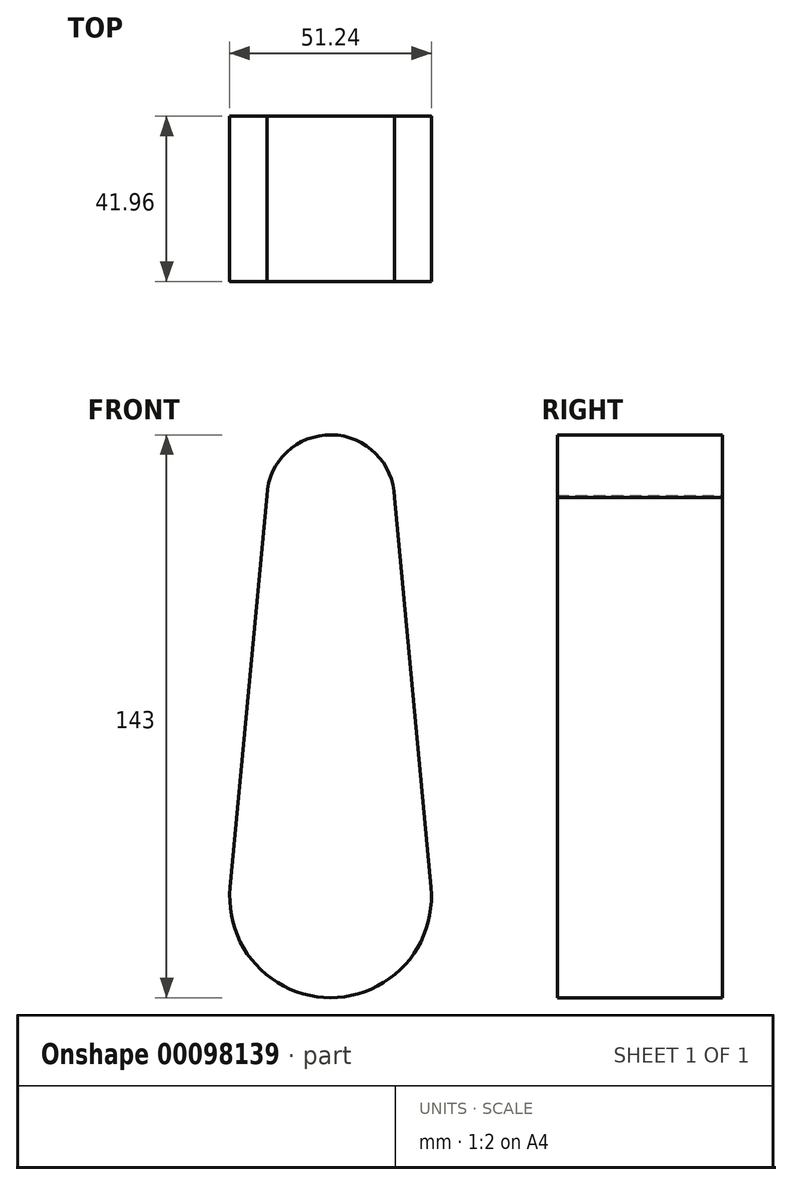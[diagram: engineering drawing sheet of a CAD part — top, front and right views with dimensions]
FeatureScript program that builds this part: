
annotation { "Feature Type Name" : "Feature", "Feature Type Description" : "" }
export const myFeature = defineFeature(function(context is Context, id is Id, definition is map)
    precondition{}
    {
        {
            var Q0;
            Q0=qCreatedBy(makeId("Front.planeOp"),FACE);
            var sketch = newSketch(context, id + "F0", { "sketchPlane" : qUnion([Q0])});
            skCircle(sketch, "E0", {"center": v(0, 55.57) * mm, "radius": 16.22 * mm});
            skCircle(sketch, "E1", {"center": v(0, -45.59) * mm, "radius": 25.62 * mm});
            skLineSegment(sketch, "E2", {"start": v(-16.2, 56.33) * mm, "end": v(-25.5, -43.2) * mm});
            skLineSegment(sketch, "E3", {"start": v(16.22, 55.84) * mm, "end": v(25.5, -43.2) * mm});
            skSolve(sketch);
        }
        {
            var Q0;
            Q0 = qSketchRegion(id + "F0", true);
            extrude(context, id + "F1", {"entities" : qUnion([Q0]), "depth" : 41.96 * mm});
        }
    });
